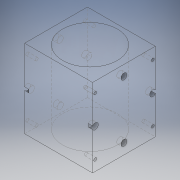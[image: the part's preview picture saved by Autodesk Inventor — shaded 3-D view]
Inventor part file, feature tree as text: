
AUTODESK INVENTOR PART (.ipt)
format: ipt  version: 2016 (Build 200138000, 138)  size: 193,024 bytes
history: native  units: in
note: dims shown in document units (in); Inventor stores cm internally (conversion verified against a paired STEP export)
features: extrude x6, sketch x6
ambient origin geometry x8: Origin, YZ Plane, XZ Plane, XY Plane, X Axis, Y Axis, Z Axis, Center Point
bodies: Solid1 (feature_tree)
feature tree (12):
  extrude  "block"  Depth=3.0in
  extrude  "hole"  Depth=3.75in
  sketch  "Sketch4"  dims[d8=3.5in d9=0.0in d10=3.0in]
  extrude  "Extrusion3"  Depth=3.0in
  extrude  "Extrusion4"  Depth=3.0in
  extrude  "Extrusion5"  Depth=3.0in
  extrude  "Extrusion6"  Depth=0.45in
  sketch  "Sketch1"  dims[d3=3.25in d4=3.0in]
  sketch  "Sketch2"  dims[d5=3.75in d6=0.0in d7=2.61in]
  sketch  "Sketch5"  dims[d11=3.0in d21=0.125in]
  sketch  "Sketch6"  dims[d24=3.0in d25=3.0in d26=0.125in d27=0.125in d28=0.125in d29=0.125in d30=0.29in]
  sketch  "Sketch9"  dims[d32=0.29in d33=0.29in d34=0.29in d35=0.125in d36=0.2in d37=0.0in d38=0.138in d39=0.138in d40=0.138in d41=0.138in d42=0.45in d43=0.0in d44=0.2in d45=0.0in d46=0.45in d47=0.0in]
